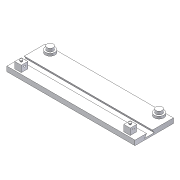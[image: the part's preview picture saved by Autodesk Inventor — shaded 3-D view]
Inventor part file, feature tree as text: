
AUTODESK INVENTOR PART (.ipt)
format: ipt  version: unknown  size: 306,688 bytes
history: native  units: mm
features: extrude x11, sketch x11, projected_geometry x2, mirror x1, pattern_linear x1
ambient origin geometry x8: Origin, YZ Plane, XZ Plane, XY Plane, X Axis, Y Axis, Z Axis, Center Point
feature tree (26):
  extrude  "Extrusion1"  Depth=2.0mm
  extrude  "Extrusion2"  Depth=3.0mm
  mirror  "Mirror1"
  extrude  "Extrusion10"  TaperAngle=0.0deg  [1 undecoded]
  extrude  "Extrusion13"  Depth=6.0mm
  extrude  "Extrusion14"  Depth=12.0mm
  extrude  "Extrusion20"  Depth=40.0mm
  extrude  "Extrusion21"  Depth=6.0mm
  extrude  "Extrusion22"  Depth=3.0mm
  extrude  "Extrusion23"  Depth=10.0mm TaperAngle=0.0deg
  extrude  "Extrusion24"  Depth=4.0mm
  pattern_linear  "Rectangular Pattern1"  Spacing1=12.0mm  [1 undecoded]
  extrude  "Extrusion25"  Depth=4.0mm
  sketch  "Sketch1"  dims[d11=3.0mm d12=0.0mm d15=2.0mm]
  sketch  "Sketch2"  dims[d19=60.0deg d20=3.0mm]
  sketch  "Sketch11"  dims[d21=30.0mm d22=0.0mm d65=0.0mm]
  projected_geometry  "Projected Loop1"
  sketch  "Sketch14"  dims[d67=6.0mm d68=6.0mm]
  projected_geometry  "Projected Loop2"
  sketch  "Sketch15"  dims[d69=1.5mm d70=0.0mm d75=12.0mm]
  sketch  "Sketch21"  dims[d76=12.0mm d77=40.0mm]
  sketch  "Sketch22"  dims[d78=30.0mm d84=6.0mm]
  sketch  "Sketch23"  dims[d85=6.0mm d86=3.0mm]
  sketch  "Sketch24"  dims[d87=0.0mm d88=10.0mm d89=0.0mm]
  sketch  "Sketch25"  dims[d90=4.0mm d91=4.0mm]
  sketch  "Sketch26"  dims[d92=2.0mm d93=0.0mm d120=12.0mm d121=4.0mm d122=4.0mm d123=0.0mm d124=10.0mm d125=0.0mm d126=1.0mm d127=2.5mm d128=10.0mm d129=0.0mm d130=1.0mm d131=0.5mm d132=0.0mm d133=0.8mm d134=0.5mm d135=0.0mm d136=20.0mm d138=68.0mm d139=6.0mm d140=0.0mm]
note: 2 required parameter values undecoded (feature->parameter linkage not recoverable at this tier; creation-order binding heuristic only, values carry confidence <= 0.55)
